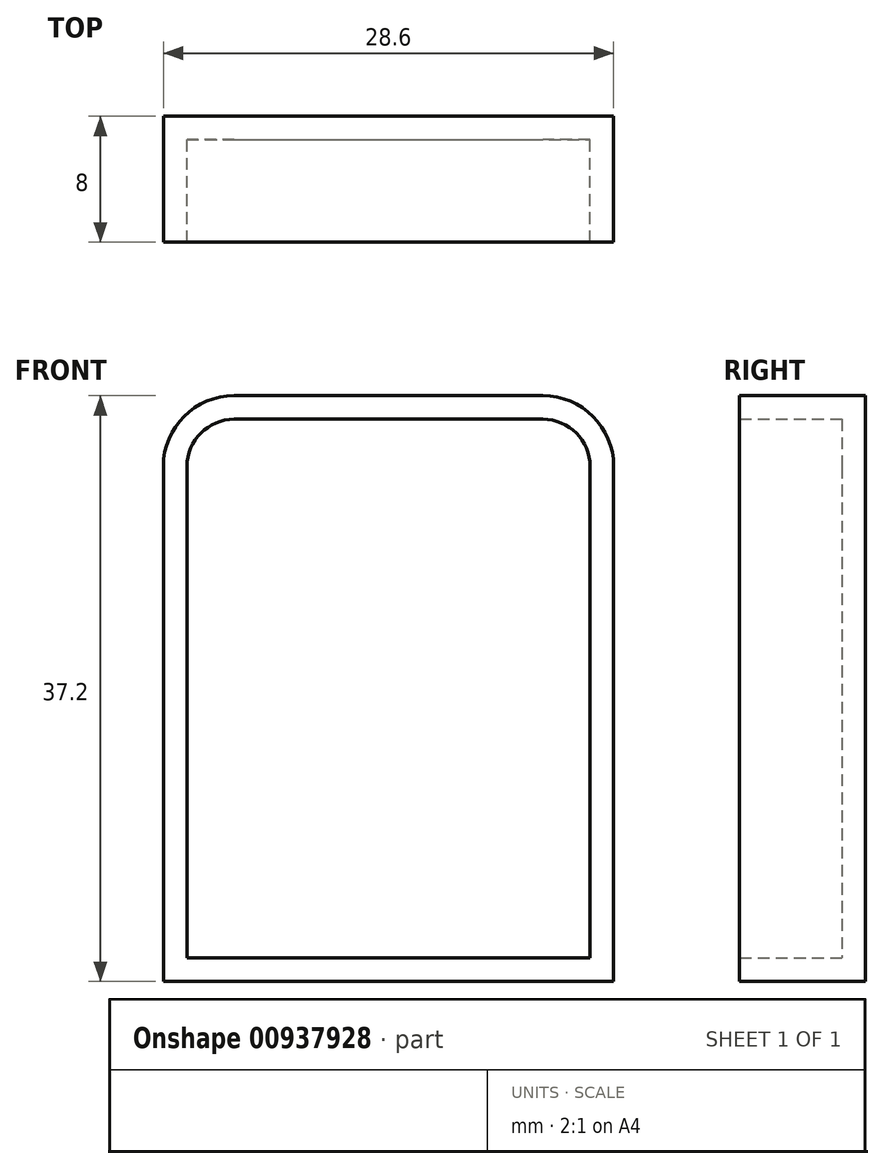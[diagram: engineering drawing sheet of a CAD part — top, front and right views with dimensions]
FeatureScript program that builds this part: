
annotation { "Feature Type Name" : "Feature", "Feature Type Description" : "" }
export const myFeature = defineFeature(function(context is Context, id is Id, definition is map)
    precondition{}
    {
        {
            var Q0;
            Q0=qCreatedBy(makeId("Front.planeOp"),FACE);
            var sketch = newSketch(context, id + "F0", { "sketchPlane" : qUnion([Q0])});
            skLineSegment(sketch, "E0.bottom", {"start": v(-22.6, 34.2) * mm, "end": v(-3, 34.2) * mm});
            skLineSegment(sketch, "E0.top", {"start": v(-25.6, 0) * mm, "end": v(0, 0) * mm});
            skLineSegment(sketch, "E0.left", {"start": v(-25.6, 31.2) * mm, "end": v(-25.6, 0) * mm});
            skLineSegment(sketch, "E0.right", {"start": v(0, 31.2) * mm, "end": v(0, 0) * mm});
            skPoint(sketch, "E1.visualSharp", {"position": v(-25.6, 34.2) * mm});
            skArc(sketch, "E1.filletArc", {"start": v(-22.6, 34.2) * mm, "mid": v(-24.72, 33.32) * mm, "end": v(-25.6, 31.2) * mm});
            skPoint(sketch, "E2.visualSharp", {"position": v(0, 34.2) * mm});
            skArc(sketch, "E2.filletArc", {"start": v(0, 31.2) * mm, "mid": v(-0.88, 33.32) * mm, "end": v(-3, 34.2) * mm});
            skLineSegment(sketch, "E3", {"start": v(-27.1, -1.5) * mm, "end": v(1.5, -1.5) * mm});
            skLineSegment(sketch, "E4", {"start": v(1.5, -1.5) * mm, "end": v(1.5, 31.2) * mm});
            skLineSegment(sketch, "E5", {"start": v(-3, 35.7) * mm, "end": v(-22.6, 35.7) * mm});
            skLineSegment(sketch, "E6", {"start": v(-27.1, -1.5) * mm, "end": v(-27.1, 31.2) * mm});
            skPoint(sketch, "E7.visualSharp", {"position": v(1.5, 35.7) * mm});
            skArc(sketch, "E7.filletArc", {"start": v(1.5, 31.2) * mm, "mid": v(0.18, 34.38) * mm, "end": v(-3, 35.7) * mm});
            skPoint(sketch, "E8.visualSharp", {"position": v(-27.1, 35.7) * mm});
            skArc(sketch, "E8.filletArc", {"start": v(-22.6, 35.7) * mm, "mid": v(-25.78, 34.38) * mm, "end": v(-27.1, 31.2) * mm});
            skLineSegment(sketch, "E9", {"start": v(-12.8, -17.14) * mm, "end": v(-12.8, 40.07) * mm, "construction": true});
            skLineSegment(sketch, "E10", {"start": v(-37, 17.1) * mm, "end": v(14.36, 17.1) * mm, "construction": true});
            skSolve(sketch);
        }
        {
            var Q0;
            {var subQ0=sQuery(id+"F0.wireOp",EDGE,"GXgfUGaT-lgrT-AhyM-uQlN-o11690qivSne.top");Q0=makeQuery(id+"F0.imprint","IMPRINT",FACE,{"disambiguationData":[TD([[makeQuery(id+"F0.imprint","IMPRINT",EDGE,{"derivedFrom":subQ0}),-1.0]])]});}
            var Q1;
            {var subQ0=sQuery(id+"F0.wireOp",EDGE,"GXgfUGaT-lgrT-AhyM-uQlN-o11690qivSne.bottom");Q1=makeQuery(id+"F0.imprint","IMPRINT",FACE,{"disambiguationData":[TD([[makeQuery(id+"F0.imprint","IMPRINT",EDGE,{"derivedFrom":subQ0}),1.0]])]});}
            var Q2;
            {var subQ0=sQuery(id+"F0.wireOp",EDGE,"f976d2f9-4800-4454-9d82-1ee03783d21f0.MirrorCS");Q2=makeQuery(id+"F0.imprint","IMPRINT",FACE,{"disambiguationData":[TD([[makeQuery(id+"F0.imprint","IMPRINT",EDGE,{"derivedFrom":subQ0}),1.0]])]});}
            var Q3;
            {var subQ0=sQuery(id+"F0.wireOp",EDGE,"1cf12fce-86e8-4bcd-8b75-419f3d70dd0d0.MirrorCS");Q3=makeQuery(id+"F0.imprint","IMPRINT",FACE,{"disambiguationData":[TD([[makeQuery(id+"F0.imprint","IMPRINT",EDGE,{"derivedFrom":subQ0}),-1.0]])]});}
            var Q4;
            Q4=makeQuery(id+"F0.imprint","IMPRINT",FACE,{"disambiguationData":[TD([[makeQuery(id+"F0.imprint","IMPRINT",EDGE,{"derivedFrom":sQuery(id+"F0.wireOp",EDGE,"E0.bottom")}),1.0]])]});
            extrude(context, id + "F1", {"entities" : qUnion([Q0, Q1, Q2, Q3, Q4]), "depth" : 8 * mm, "offsetDistance" : 25 * mm});
        }
        {
            var Q0;
            Q0=makeQuery(id+"F0.imprint","IMPRINT",FACE,{"disambiguationData":[TD([[makeQuery(id+"F0.imprint","IMPRINT",EDGE,{"derivedFrom":sQuery(id+"F0.wireOp",EDGE,"GXgfUGaT-lgrT-AhyM-uQlN-o11690qivSne.bottom")}),-1.0]])]});
            var Q1;
            {var subQ1=sQuery(id+"F0.wireOp",EDGE,"2c6e4e1a-9b57-41c1-be55-0c207e2d755d0.MirrorCS");Q1=makeQuery(id+"F0.imprint","IMPRINT",FACE,{"disambiguationData":[TD([[makeQuery(id+"F0.imprint","IMPRINT",EDGE,{"derivedFrom":subQ1}),1.0]])]});}
            var Q2;
            Q2=makeQuery(id+"F0.imprint","IMPRINT",FACE,{"disambiguationData":[TD([[makeQuery(id+"F0.imprint","IMPRINT",EDGE,{"derivedFrom":sQuery(id+"F0.wireOp",EDGE,"E0.bottom")}),-1.0]])]});
            extrude(context, id + "F2", {"entities" : qUnion([Q0, Q1, Q2]), "operationType" : NewBodyOperationType.ADD, "depth" : 1.5 * mm, "offsetDistance" : 25 * mm});
        }
    });
